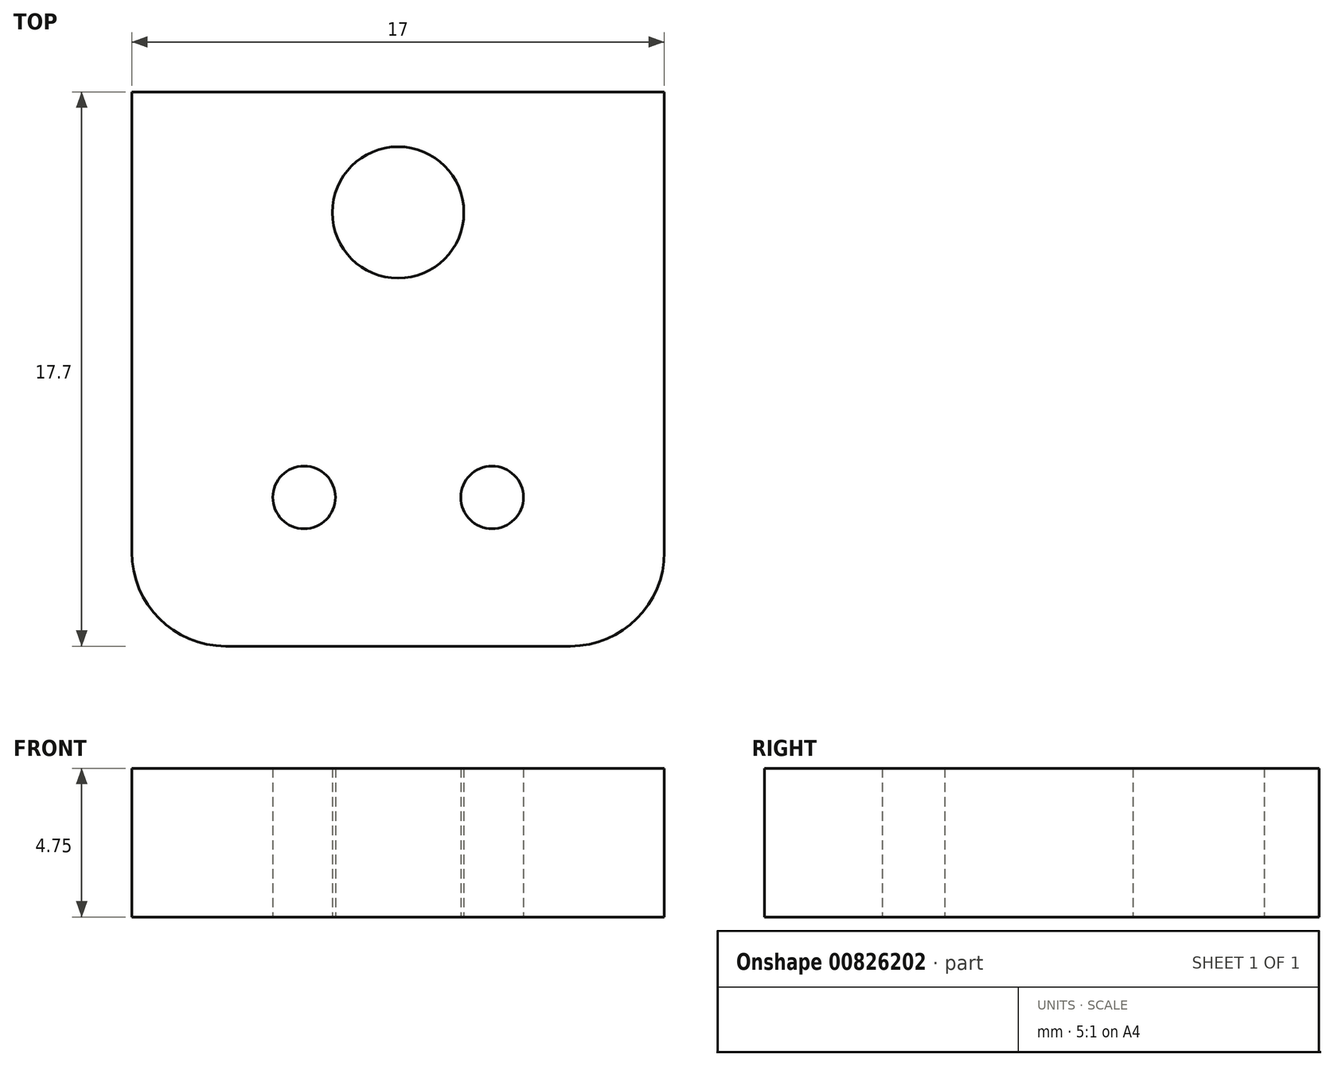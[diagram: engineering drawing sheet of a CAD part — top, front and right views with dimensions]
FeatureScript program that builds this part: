
annotation { "Feature Type Name" : "Feature", "Feature Type Description" : "" }
export const myFeature = defineFeature(function(context is Context, id is Id, definition is map)
    precondition{}
    {
        {
            var Q0;
            Q0=qCreatedBy(makeId("Top.planeOp"),FACE);
            var sketch = newSketch(context, id + "F0", { "sketchPlane" : qUnion([Q0])});
            skLineSegment(sketch, "E0.bottom", {"start": v(8.5, -8.85) * mm, "end": v(-8.5, -8.85) * mm});
            skLineSegment(sketch, "E0.top", {"start": v(8.5, 8.85) * mm, "end": v(-8.5, 8.85) * mm});
            skLineSegment(sketch, "E0.left", {"start": v(8.5, -8.85) * mm, "end": v(8.5, 8.85) * mm});
            skLineSegment(sketch, "E0.right", {"start": v(-8.5, -8.85) * mm, "end": v(-8.5, 8.85) * mm});
            skPoint(sketch, "E0.middle", {"position": v(0, 0) * mm});
            skCircle(sketch, "E1", {"center": v(0, 5) * mm, "radius": 2.1 * mm});
            skLineSegment(sketch, "E2", {"start": v(-8.5, 1.15) * mm, "end": v(8.5, 1.15) * mm, "construction": true});
            skLineSegment(sketch, "E3", {"start": v(-8.5, -8.85) * mm, "end": v(8.5, -8.85) * mm, "construction": true});
            skLineSegment(sketch, "E4", {"start": v(0, 1.15) * mm, "end": v(0, -8.85) * mm, "construction": true});
            skCircle(sketch, "E5", {"center": v(3, -4.1) * mm, "radius": 1 * mm});
            skCircle(sketch, "E6.MirrorC", {"center": v(-3, -4.1) * mm, "radius": 1 * mm});
            skSolve(sketch);
        }
        {
            var Q0;
            Q0=makeQuery(id+"F0.imprint","IMPRINT",FACE,{"disambiguationData":[TD([[makeQuery(id+"F0.imprint","IMPRINT",EDGE,{"derivedFrom":sQuery(id+"F0.wireOp",EDGE,"E0.bottom")}),-1.0]])]});
            extrude(context, id + "F1", {"entities" : qUnion([Q0]), "depth" : 4.75 * mm, "offsetDistance" : 25 * mm});
        }
        {
            var Q0;
            Q0=makeQuery(id+"F1.opExtrude","SWEPT_EDGE",EDGE,{"disambiguationData":[OSD([sQuery(id+"F0.wireOp",EDGE,"E0.bottom"),sQuery(id+"F0.wireOp",EDGE,"E0.right")])]});
            var Q1;
            Q1=makeQuery(id+"F1.opExtrude","SWEPT_EDGE",EDGE,{"disambiguationData":[OSD([sQuery(id+"F0.wireOp",EDGE,"E0.bottom"),sQuery(id+"F0.wireOp",EDGE,"E0.left")])]});
            fillet(context, id + "F2", {"entities" : qUnion([Q0, Q1]), "radius" : 3 * mm, "tangentPropagation" : true, "allowEdgeOverflow" : false});
        }
    });
